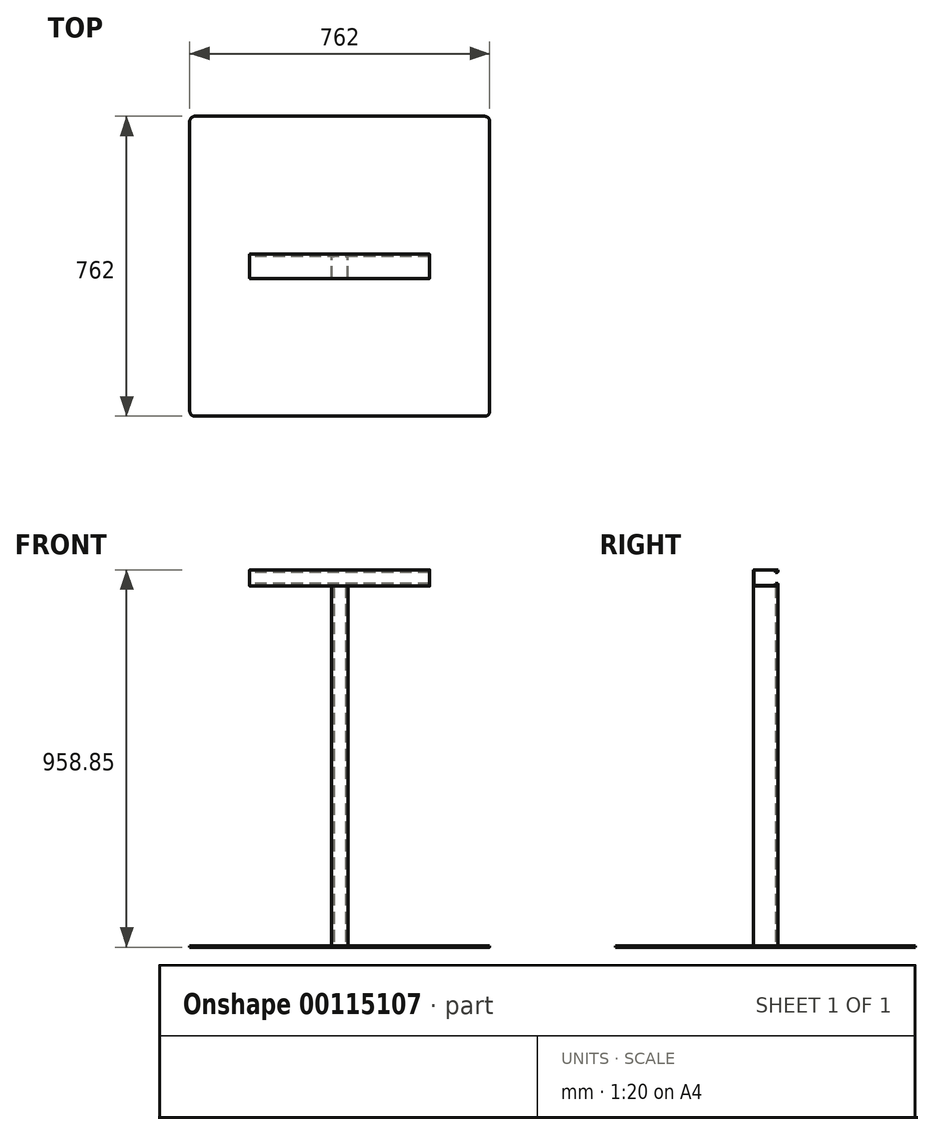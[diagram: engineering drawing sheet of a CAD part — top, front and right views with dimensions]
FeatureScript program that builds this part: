
annotation { "Feature Type Name" : "Feature", "Feature Type Description" : "" }
export const myFeature = defineFeature(function(context is Context, id is Id, definition is map)
    precondition{}
    {
        {
            var Q0;
            Q0=qCreatedBy(makeId("Top.planeOp"),FACE);
            var sketch = newSketch(context, id + "F0", { "sketchPlane" : qUnion([Q0])});
            skLineSegment(sketch, "E0", {"start": v(0, -30.96) * mm, "end": v(19.37, -30.96) * mm});
            skLineSegment(sketch, "E1", {"start": v(20.64, -29.69) * mm, "end": v(20.64, 29.69) * mm});
            skLineSegment(sketch, "E2", {"start": v(19.37, 30.96) * mm, "end": v(15.56, 30.96) * mm});
            skLineSegment(sketch, "E3", {"start": v(14.29, 29.69) * mm, "end": v(14.29, 24.6) * mm});
            skLineSegment(sketch, "E4", {"start": v(0, 0) * mm, "end": v(20.64, 0) * mm, "construction": true});
            skLineSegment(sketch, "E5", {"start": v(0, 0) * mm, "end": v(0, -30.96) * mm, "construction": true});
            skLineSegment(sketch, "E6.MirrorCS", {"start": v(0, -30.96) * mm, "end": v(-19.37, -30.96) * mm});
            skLineSegment(sketch, "E7.MirrorCS", {"start": v(-19.37, 30.96) * mm, "end": v(-15.56, 30.96) * mm});
            skLineSegment(sketch, "E8.MirrorCS", {"start": v(-20.64, -29.69) * mm, "end": v(-20.64, 29.69) * mm});
            skLineSegment(sketch, "E9.MirrorCS", {"start": v(-14.29, 29.69) * mm, "end": v(-14.29, 24.6) * mm});
            skPoint(sketch, "E10.visualSharp", {"position": v(-20.64, 30.96) * mm});
            skArc(sketch, "E10.filletArc", {"start": v(-19.37, 30.96) * mm, "mid": v(-20.27, 30.58) * mm, "end": v(-20.64, 29.69) * mm});
            skPoint(sketch, "E11.visualSharp", {"position": v(-14.29, 30.96) * mm});
            skArc(sketch, "E11.filletArc", {"start": v(-14.29, 29.69) * mm, "mid": v(-14.66, 30.58) * mm, "end": v(-15.56, 30.96) * mm});
            skPoint(sketch, "E12.visualSharp", {"position": v(14.29, 30.96) * mm});
            skArc(sketch, "E12.filletArc", {"start": v(15.56, 30.96) * mm, "mid": v(14.66, 30.58) * mm, "end": v(14.29, 29.69) * mm});
            skPoint(sketch, "E13.visualSharp", {"position": v(20.64, 30.96) * mm});
            skArc(sketch, "E13.filletArc", {"start": v(20.64, 29.69) * mm, "mid": v(20.27, 30.58) * mm, "end": v(19.37, 30.96) * mm});
            skPoint(sketch, "E14.visualSharp", {"position": v(20.64, -30.96) * mm});
            skArc(sketch, "E14.filletArc", {"start": v(19.37, -30.96) * mm, "mid": v(20.27, -30.58) * mm, "end": v(20.64, -29.69) * mm});
            skPoint(sketch, "E15.visualSharp", {"position": v(-20.64, -30.96) * mm});
            skArc(sketch, "E15.filletArc", {"start": v(-20.64, -29.69) * mm, "mid": v(-20.27, -30.58) * mm, "end": v(-19.37, -30.96) * mm});
            skLineSegment(sketch, "E16.0", {"start": v(15.3, 29.69) * mm, "end": v(15.3, 24.6) * mm});
            skArc(sketch, "E16.1", {"start": v(15.56, 29.95) * mm, "mid": v(15.37, 29.87) * mm, "end": v(15.3, 29.69) * mm});
            skLineSegment(sketch, "E16.2", {"start": v(19.37, 29.95) * mm, "end": v(15.56, 29.95) * mm});
            skArc(sketch, "E16.3", {"start": v(19.63, 29.69) * mm, "mid": v(19.55, 29.87) * mm, "end": v(19.37, 29.95) * mm});
            skArc(sketch, "E16.4", {"start": v(-19.37, 29.95) * mm, "mid": v(-19.55, 29.87) * mm, "end": v(-19.63, 29.69) * mm});
            skLineSegment(sketch, "E16.5", {"start": v(-19.37, 29.95) * mm, "end": v(-15.56, 29.95) * mm});
            skArc(sketch, "E16.6", {"start": v(-15.3, 29.69) * mm, "mid": v(-15.37, 29.87) * mm, "end": v(-15.56, 29.95) * mm});
            skLineSegment(sketch, "E16.7", {"start": v(-15.3, 29.69) * mm, "end": v(-15.3, 24.6) * mm});
            skLineSegment(sketch, "E16.8", {"start": v(-19.63, -29.69) * mm, "end": v(-19.63, 29.69) * mm});
            skArc(sketch, "E16.9", {"start": v(-19.63, -29.69) * mm, "mid": v(-19.55, -29.87) * mm, "end": v(-19.37, -29.95) * mm});
            skLineSegment(sketch, "E16.10", {"start": v(0, -29.95) * mm, "end": v(-19.37, -29.95) * mm});
            skLineSegment(sketch, "E16.11", {"start": v(0, -29.95) * mm, "end": v(19.37, -29.95) * mm});
            skArc(sketch, "E16.12", {"start": v(19.37, -29.95) * mm, "mid": v(19.55, -29.87) * mm, "end": v(19.63, -29.69) * mm});
            skLineSegment(sketch, "E16.13", {"start": v(19.63, -29.69) * mm, "end": v(19.63, 29.69) * mm});
            skLineSegment(sketch, "E17", {"start": v(-15.3, 24.6) * mm, "end": v(-14.29, 24.6) * mm});
            skLineSegment(sketch, "E18", {"start": v(14.29, 24.6) * mm, "end": v(15.3, 24.6) * mm});
            skSolve(sketch);
        }
        {
            var Q0;
            Q0 = qSketchRegion(id + "F0", true);
            extrude(context, id + "F1", {"entities" : qUnion([Q0]), "depth" : 914.4 * mm});
        }
        {
            var Q0;
            Q0=qCreatedBy(makeId("Top.planeOp"),FACE);
            var sketch = newSketch(context, id + "F2", { "sketchPlane" : qUnion([Q0])});
            skLineSegment(sketch, "E19.bottom", {"start": v(381, -381) * mm, "end": v(-381, -381) * mm});
            skLineSegment(sketch, "E19.top", {"start": v(381, 381) * mm, "end": v(-381, 381) * mm});
            skLineSegment(sketch, "E19.left", {"start": v(381, -381) * mm, "end": v(381, 381) * mm});
            skLineSegment(sketch, "E19.right", {"start": v(-381, -381) * mm, "end": v(-381, 381) * mm});
            skPoint(sketch, "E19.middle", {"position": v(0, 0) * mm});
            skSolve(sketch);
        }
        {
            var Q0;
            Q0 = qSketchRegion(id + "F2", true);
            extrude(context, id + "F3", {"entities" : qUnion([Q0]), "operationType" : NewBodyOperationType.ADD, "oppositeDirection" : true, "depth" : 3.17 * mm});
        }
        {
            var Q0;
            Q0=makeQuery(id+"F3.opExtrude","SWEPT_EDGE",EDGE,{"disambiguationData":[OSD([sQuery(id+"F2.wireOp",EDGE,"E19.bottom"),sQuery(id+"F2.wireOp",EDGE,"E19.left")])]});
            var Q1;
            Q1=makeQuery(id+"F3.opExtrude","SWEPT_EDGE",EDGE,{"disambiguationData":[OSD([sQuery(id+"F2.wireOp",EDGE,"E19.top"),sQuery(id+"F2.wireOp",EDGE,"E19.left")])]});
            var Q2;
            Q2=makeQuery(id+"F3.opExtrude","SWEPT_EDGE",EDGE,{"disambiguationData":[OSD([sQuery(id+"F2.wireOp",EDGE,"E19.top"),sQuery(id+"F2.wireOp",EDGE,"E19.right")])]});
            var Q3;
            Q3=makeQuery(id+"F3.opExtrude","SWEPT_EDGE",EDGE,{"disambiguationData":[OSD([sQuery(id+"F2.wireOp",EDGE,"E19.bottom"),sQuery(id+"F2.wireOp",EDGE,"E19.right")])]});
            fillet(context, id + "F4", {"entities" : qUnion([Q0, Q1, Q2, Q3]), "radius" : 12.7 * mm, "tangentPropagation" : true, "allowEdgeOverflow" : false});
        }
        {
            var Q0;
            Q0=qCreatedBy(makeId("Right.planeOp"),FACE);
            var sketch = newSketch(context, id + "F5", { "sketchPlane" : qUnion([Q0])});
            skLineSegment(sketch, "E20.MirrorCS", {"start": v(-29.95, 954.4) * mm, "end": v(-29.95, 915.67) * mm});
            skArc(sketch, "E21.MirrorCS", {"start": v(-29.69, 914.4) * mm, "mid": v(-30.58, 914.77) * mm, "end": v(-30.96, 915.67) * mm});
            skArc(sketch, "E22.MirrorCS", {"start": v(29.69, 954.67) * mm, "mid": v(29.87, 954.6) * mm, "end": v(29.95, 954.4) * mm});
            skArc(sketch, "E23.MirrorCS", {"start": v(-29.69, 915.4) * mm, "mid": v(-29.87, 915.48) * mm, "end": v(-29.95, 915.67) * mm});
            skArc(sketch, "E24.MirrorCS", {"start": v(29.69, 955.68) * mm, "mid": v(30.58, 955.3) * mm, "end": v(30.96, 954.4) * mm});
            skArc(sketch, "E25.MirrorCS", {"start": v(29.95, 950.6) * mm, "mid": v(29.87, 950.4) * mm, "end": v(29.69, 950.33) * mm});
            skLineSegment(sketch, "E26.MirrorCS", {"start": v(29.95, 954.4) * mm, "end": v(29.95, 950.6) * mm});
            skArc(sketch, "E27.MirrorCS", {"start": v(30.96, 950.6) * mm, "mid": v(30.58, 949.7) * mm, "end": v(29.69, 949.33) * mm});
            skLineSegment(sketch, "E28.MirrorCS", {"start": v(30.96, 954.4) * mm, "end": v(30.96, 950.6) * mm});
            skArc(sketch, "E29.MirrorCS", {"start": v(29.69, 919.74) * mm, "mid": v(29.87, 919.67) * mm, "end": v(29.95, 919.48) * mm});
            skArc(sketch, "E30.MirrorCS", {"start": v(29.69, 920.75) * mm, "mid": v(30.58, 920.38) * mm, "end": v(30.96, 919.48) * mm});
            skArc(sketch, "E31.MirrorCS", {"start": v(30.96, 915.67) * mm, "mid": v(30.58, 914.77) * mm, "end": v(29.69, 914.4) * mm});
            skLineSegment(sketch, "E32.MirrorCS", {"start": v(30.96, 915.67) * mm, "end": v(30.96, 919.48) * mm});
            skLineSegment(sketch, "E33.MirrorCS", {"start": v(29.95, 915.67) * mm, "end": v(29.95, 919.48) * mm});
            skArc(sketch, "E34.MirrorCS", {"start": v(29.95, 915.67) * mm, "mid": v(29.87, 915.48) * mm, "end": v(29.69, 915.4) * mm});
            skArc(sketch, "E35.MirrorCS", {"start": v(-30.96, 954.4) * mm, "mid": v(-30.58, 955.3) * mm, "end": v(-29.69, 955.68) * mm});
            skArc(sketch, "E36.MirrorCS", {"start": v(-29.95, 954.4) * mm, "mid": v(-29.87, 954.6) * mm, "end": v(-29.69, 954.67) * mm});
            skLineSegment(sketch, "E37.MirrorCS", {"start": v(29.69, 919.74) * mm, "end": v(24.6, 919.74) * mm});
            skLineSegment(sketch, "E38.MirrorCS", {"start": v(24.6, 919.74) * mm, "end": v(24.6, 920.75) * mm});
            skLineSegment(sketch, "E39.MirrorCS", {"start": v(29.69, 920.75) * mm, "end": v(24.6, 920.75) * mm});
            skLineSegment(sketch, "E40.MirrorCS", {"start": v(24.6, 949.33) * mm, "end": v(24.6, 950.33) * mm});
            skLineSegment(sketch, "E41.MirrorCS", {"start": v(29.69, 950.33) * mm, "end": v(24.6, 950.33) * mm});
            skLineSegment(sketch, "E42.MirrorCS", {"start": v(29.69, 949.32) * mm, "end": v(24.6, 949.32) * mm});
            skLineSegment(sketch, "E43.MirrorCS", {"start": v(-29.69, 954.67) * mm, "end": v(29.69, 954.67) * mm});
            skPoint(sketch, "E44.MirrorP", {"position": v(30.96, 914.4) * mm});
            skLineSegment(sketch, "E45.MirrorCS", {"start": v(0, 935.04) * mm, "end": v(0, 955.68) * mm, "construction": true});
            skLineSegment(sketch, "E46.MirrorCS", {"start": v(0, 935.04) * mm, "end": v(-30.96, 935.04) * mm, "construction": true});
            skLineSegment(sketch, "E47.MirrorCS", {"start": v(-30.96, 935.04) * mm, "end": v(-30.96, 954.4) * mm});
            skPoint(sketch, "E48.MirrorP", {"position": v(-30.96, 914.4) * mm});
            skPoint(sketch, "E49.MirrorP", {"position": v(30.96, 955.68) * mm});
            skLineSegment(sketch, "E50.MirrorCS", {"start": v(-29.69, 914.4) * mm, "end": v(29.69, 914.4) * mm});
            skPoint(sketch, "E51.MirrorP", {"position": v(30.96, 920.75) * mm});
            skLineSegment(sketch, "E52.MirrorCS", {"start": v(-29.69, 955.68) * mm, "end": v(29.69, 955.68) * mm});
            skPoint(sketch, "E53.MirrorP", {"position": v(30.96, 949.33) * mm});
            skLineSegment(sketch, "E54.MirrorCS", {"start": v(-30.96, 935.04) * mm, "end": v(-30.96, 915.67) * mm});
            skLineSegment(sketch, "E55.MirrorCS", {"start": v(-29.69, 915.4) * mm, "end": v(29.69, 915.4) * mm});
            skSolve(sketch);
        }
        {
            var Q0;
            Q0 = qSketchRegion(id + "F5", true);
            extrude(context, id + "F6", {"entities" : qUnion([Q0]), "operationType" : NewBodyOperationType.ADD, "endBound" : BoundingType.SYMMETRIC, "depth" : 457.2 * mm});
        }
    });
